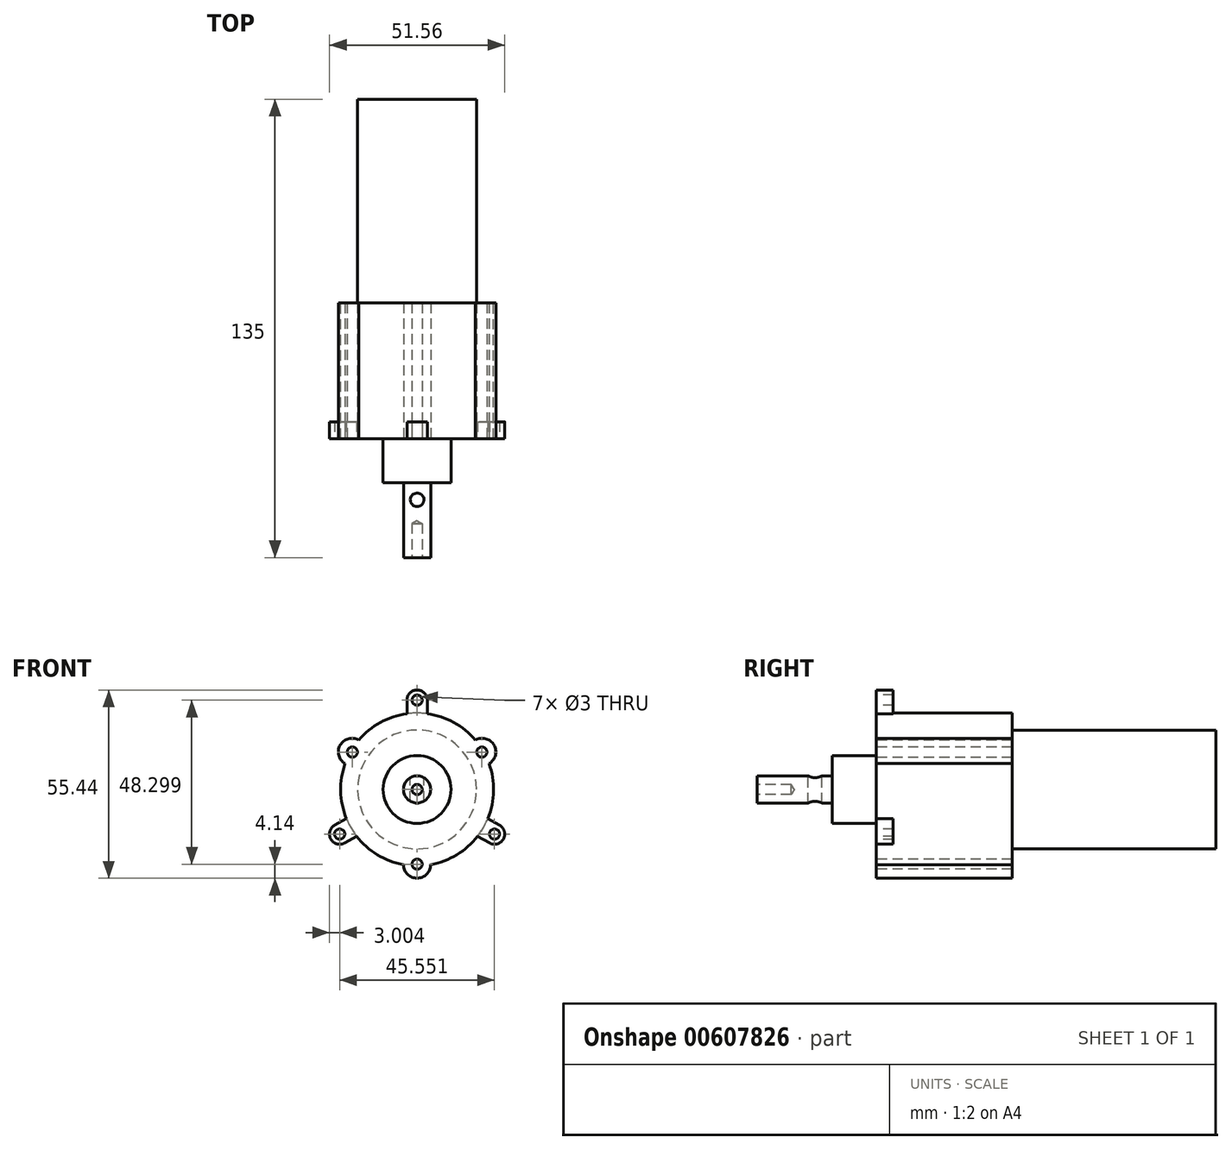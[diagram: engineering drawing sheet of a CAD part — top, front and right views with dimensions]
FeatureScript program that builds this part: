
annotation { "Feature Type Name" : "Feature", "Feature Type Description" : "" }
export const myFeature = defineFeature(function(context is Context, id is Id, definition is map)
    precondition{}
    {
        {
            var Q0;
            Q0=qCreatedBy(makeId("Front.planeOp"),FACE);
            var sketch = newSketch(context, id + "F0", { "sketchPlane" : qUnion([Q0])});
            skCircle(sketch, "E0", {"center": v(0, 0) * mm, "radius": 17.5 * mm});
            skSolve(sketch);
        }
        {
            var Q0;
            Q0 = qSketchRegion(id + "F0", true);
            extrude(context, id + "F1", {"entities" : qUnion([Q0]), "depth" : 60 * mm, "offsetDistance" : 25 * mm});
        }
        {
            var Q0;
            Q0=makeQuery(id+"F1.opExtrude","CAP_FACE",FACE,{"disambiguationData":[OSD([sQuery(id+"F0.wireOp",EDGE,"E0")])],"isStart":false});
            var sketch = newSketch(context, id + "F2", { "sketchPlane" : qUnion([Q0])});
            skCircle(sketch, "E1", {"center": v(0, 0) * mm, "radius": 22.5 * mm});
            skSolve(sketch);
        }
        {
            var Q0;
            Q0 = qSketchRegion(id + "F2", true);
            extrude(context, id + "F3", {"entities" : qUnion([Q0]), "operationType" : NewBodyOperationType.ADD, "depth" : 40 * mm, "offsetDistance" : 25 * mm});
        }
        {
            var Q0;
            Q0=makeQuery(id+"F3.opExtrude","CAP_FACE",FACE,{"disambiguationData":[OSD([sQuery(id+"F2.wireOp",EDGE,"E1")])],"isStart":false});
            var sketch = newSketch(context, id + "F4", { "sketchPlane" : qUnion([Q0])});
            skLineSegment(sketch, "E2", {"start": v(0, 0) * mm, "end": v(0, -22.5) * mm, "construction": true});
            skLineSegment(sketch, "E3", {"start": v(-4, -22.14) * mm, "end": v(4, -22.14) * mm});
            skArc(sketch, "E4", {"start": v(-4, -22.14) * mm, "mid": v(0, -26.14) * mm, "end": v(4, -22.14) * mm});
            skArc(sketch, "E5.1.0", {"start": v(21.18, 7.6) * mm, "mid": v(22.64, 13.07) * mm, "end": v(17.18, 14.53) * mm});
            skLineSegment(sketch, "E5.1.1", {"start": v(21.18, 7.6) * mm, "end": v(17.18, 14.53) * mm});
            skArc(sketch, "E5.2.0", {"start": v(-17.18, 14.53) * mm, "mid": v(-22.64, 13.07) * mm, "end": v(-21.18, 7.6) * mm});
            skLineSegment(sketch, "E5.2.1", {"start": v(-17.18, 14.53) * mm, "end": v(-21.18, 7.6) * mm});
            skPoint(sketch, "E5.center", {"position": v(0, 0) * mm});
            skSolve(sketch);
        }
        {
            var Q0;
            Q0 = qSketchRegion(id + "F4", true);
            extrude(context, id + "F5", {"entities" : qUnion([Q0]), "operationType" : NewBodyOperationType.ADD, "oppositeDirection" : true, "depth" : 40 * mm, "offsetDistance" : 25 * mm});
        }
        {
            var Q0;
            Q0=makeQuery(id+"F5.boolean.opBoolean","MERGE",FACE,{"derivedFrom":[makeQuery(id+"F3.opExtrude","CAP_FACE",FACE,{"disambiguationData":[OSD([sQuery(id+"F2.wireOp",EDGE,"E1")])],"isStart":false}),makeQuery(id+"F5.opExtrude","CAP_FACE",FACE,{"disambiguationData":[OSD([sQuery(id+"F4.wireOp",EDGE,"E3"),sQuery(id+"F4.wireOp",EDGE,"E4")])],"isStart":true})]});
            var sketch = newSketch(context, id + "F6", { "sketchPlane" : qUnion([Q0])});
            skPoint(sketch, "E6", {"position": v(0, -22) * mm});
            skPoint(sketch, "E7.1.0", {"position": v(19.05, 11) * mm});
            skPoint(sketch, "E7.2.0", {"position": v(-19.05, 11) * mm});
            skPoint(sketch, "E7.center", {"position": v(0, 0) * mm});
            skSolve(sketch);
        }
        {
            var Q0;
            Q0=sQuery(id+"F6.wireOp",VERTEX,"E7.2.0");
            var Q1;
            Q1=sQuery(id+"F6.wireOp",VERTEX,"E6");
            var Q2;
            Q2=sQuery(id+"F6.wireOp",VERTEX,"E7.1.0");
            var Q3;
            Q3=makeQuery(id+"F1.opExtrude","SWEPT_BODY",BODY,{"disambiguationData":[OSD([sQuery(id+"F0.wireOp",EDGE,"E0")])]});
            hole(context, id + "F7", {"style" : HoleStyle.SIMPLE, "endStyle" : HoleEndStyle.THROUGH, "holeDiameter" : 3 * mm, "majorDiameter" : 5 * mm, "isTappedThrough" : true, "tappedDepth" : 12 * mm, "tapClearance" : 3, "locations" : qUnion([Q0, Q1, Q2]), "scope" : qUnion([Q3])});
        }
        {
            var Q0;
            Q0=makeQuery(id+"F3.opExtrude","CAP_FACE",FACE,{"disambiguationData":[OSD([sQuery(id+"F2.wireOp",EDGE,"E1")])],"isStart":false});
            var sketch = newSketch(context, id + "F8", { "sketchPlane" : qUnion([Q0])});
            skLineSegment(sketch, "E8", {"start": v(0, 22.5) * mm, "end": v(0, -22.5) * mm, "construction": true});
            skLineSegment(sketch, "E9", {"start": v(-22.5, 0) * mm, "end": v(22.5, 0) * mm, "construction": true});
            skLineSegment(sketch, "E10", {"start": v(-3, 22.3) * mm, "end": v(-3, 26.3) * mm});
            skLineSegment(sketch, "E11", {"start": v(3, 26.3) * mm, "end": v(3, 22.3) * mm});
            skArc(sketch, "E12", {"start": v(3, 26.3) * mm, "mid": v(0, 29.3) * mm, "end": v(-3, 26.3) * mm});
            skLineSegment(sketch, "E13", {"start": v(-3, 22.3) * mm, "end": v(3, 22.3) * mm});
            skCircle(sketch, "E14", {"center": v(0, 26.3) * mm, "radius": 1.5 * mm});
            skArc(sketch, "E15.1.0", {"start": v(-24.28, -10.55) * mm, "mid": v(-25.37, -14.65) * mm, "end": v(-21.28, -15.75) * mm});
            skCircle(sketch, "E15.1.1", {"center": v(-22.78, -13.15) * mm, "radius": 1.5 * mm});
            skLineSegment(sketch, "E15.1.2", {"start": v(-24.28, -10.55) * mm, "end": v(-20.81, -8.55) * mm});
            skLineSegment(sketch, "E15.1.3", {"start": v(-17.81, -13.75) * mm, "end": v(-21.28, -15.75) * mm});
            skLineSegment(sketch, "E15.1.4", {"start": v(-17.81, -13.75) * mm, "end": v(-20.81, -8.55) * mm});
            skArc(sketch, "E15.2.0", {"start": v(21.28, -15.75) * mm, "mid": v(25.37, -14.65) * mm, "end": v(24.28, -10.55) * mm});
            skCircle(sketch, "E15.2.1", {"center": v(22.78, -13.15) * mm, "radius": 1.5 * mm});
            skLineSegment(sketch, "E15.2.2", {"start": v(21.28, -15.75) * mm, "end": v(17.81, -13.75) * mm});
            skLineSegment(sketch, "E15.2.3", {"start": v(20.81, -8.55) * mm, "end": v(24.28, -10.55) * mm});
            skLineSegment(sketch, "E15.2.4", {"start": v(20.81, -8.55) * mm, "end": v(17.81, -13.75) * mm});
            skPoint(sketch, "E15.center", {"position": v(0, 0) * mm});
            skSolve(sketch);
        }
        {
            var Q0;
            Q0 = qSketchRegion(id + "F8", true);
            extrude(context, id + "F9", {"entities" : qUnion([Q0]), "operationType" : NewBodyOperationType.ADD, "oppositeDirection" : true, "depth" : 5 * mm, "offsetDistance" : 25 * mm});
        }
        {
            var Q0;
            Q0=makeQuery(id+"F9.boolean.opBoolean","MERGE",FACE,{"derivedFrom":[makeQuery(id+"F5.boolean.opBoolean","MERGE",FACE,{"derivedFrom":[makeQuery(id+"F3.opExtrude","CAP_FACE",FACE,{"disambiguationData":[OSD([sQuery(id+"F2.wireOp",EDGE,"E1")])],"isStart":false}),makeQuery(id+"F5.opExtrude","CAP_FACE",FACE,{"disambiguationData":[OSD([sQuery(id+"F4.wireOp",EDGE,"E3"),sQuery(id+"F4.wireOp",EDGE,"E4")])],"isStart":true}),makeQuery(id+"F5.opExtrude","CAP_FACE",FACE,{"disambiguationData":[OSD([sQuery(id+"F4.wireOp",EDGE,"E5.1.0"),sQuery(id+"F4.wireOp",EDGE,"E5.1.1")])],"isStart":true}),makeQuery(id+"F5.opExtrude","CAP_FACE",FACE,{"disambiguationData":[OSD([sQuery(id+"F4.wireOp",EDGE,"E5.2.0"),sQuery(id+"F4.wireOp",EDGE,"E5.2.1")])],"isStart":true})]}),makeQuery(id+"F9.opExtrude","CAP_FACE",FACE,{"disambiguationData":[OSD([sQuery(id+"F8.wireOp",EDGE,"E10"),sQuery(id+"F8.wireOp",EDGE,"E11"),sQuery(id+"F8.wireOp",EDGE,"E12"),sQuery(id+"F8.wireOp",EDGE,"E13"),sQuery(id+"F8.wireOp",EDGE,"E14")])],"isStart":true}),makeQuery(id+"F9.opExtrude","CAP_FACE",FACE,{"disambiguationData":[OSD([sQuery(id+"F8.wireOp",EDGE,"E15.1.0"),sQuery(id+"F8.wireOp",EDGE,"E15.1.1"),sQuery(id+"F8.wireOp",EDGE,"E15.1.2"),sQuery(id+"F8.wireOp",EDGE,"E15.1.3"),sQuery(id+"F8.wireOp",EDGE,"E15.1.4")])],"isStart":true}),makeQuery(id+"F9.opExtrude","CAP_FACE",FACE,{"disambiguationData":[OSD([sQuery(id+"F8.wireOp",EDGE,"E15.2.0"),sQuery(id+"F8.wireOp",EDGE,"E15.2.1"),sQuery(id+"F8.wireOp",EDGE,"E15.2.2"),sQuery(id+"F8.wireOp",EDGE,"E15.2.3"),sQuery(id+"F8.wireOp",EDGE,"E15.2.4")])],"isStart":true})]});
            var sketch = newSketch(context, id + "F10", { "sketchPlane" : qUnion([Q0])});
            skCircle(sketch, "E16", {"center": v(0, 0) * mm, "radius": 10 * mm});
            skSolve(sketch);
        }
        {
            var Q0;
            Q0=makeQuery(id+"F10.imprint","IMPRINT",FACE,{"disambiguationData":[TD([[makeQuery(id+"F10.imprint","IMPRINT",EDGE,{"derivedFrom":sQuery(id+"F10.wireOp",EDGE,"E16")}),1.0]])]});
            extrude(context, id + "F11", {"entities" : qUnion([Q0]), "operationType" : NewBodyOperationType.ADD, "depth" : 13 * mm, "offsetDistance" : 25 * mm});
        }
        {
            var Q0;
            Q0=makeQuery(id+"F11.opExtrude","CAP_FACE",FACE,{"disambiguationData":[OSD([sQuery(id+"F10.wireOp",EDGE,"E16")])],"isStart":false});
            var sketch = newSketch(context, id + "F12", { "sketchPlane" : qUnion([Q0])});
            skCircle(sketch, "E17", {"center": v(0, 0) * mm, "radius": 4 * mm});
            skSolve(sketch);
        }
        {
            var Q0;
            Q0=makeQuery(id+"F12.imprint","IMPRINT",FACE,{"disambiguationData":[TD([[makeQuery(id+"F12.imprint","IMPRINT",EDGE,{"derivedFrom":sQuery(id+"F12.wireOp",EDGE,"E17")}),1.0]])]});
            var Q1;
            Q1=sQuery(id+"F12.wireOp",EDGE,"E17");
            extrude(context, id + "F13", {"entities" : qUnion([Q0]), "operationType" : NewBodyOperationType.ADD, "surfaceEntities" : qUnion([Q1]), "depth" : 22 * mm, "offsetDistance" : 25 * mm});
        }
        {
            var Q0;
            Q0=makeQuery(id+"F13.opExtrude","CAP_FACE",FACE,{"disambiguationData":[OSD([sQuery(id+"F12.wireOp",EDGE,"E17")])],"isStart":false});
            var sketch = newSketch(context, id + "F14", { "sketchPlane" : qUnion([Q0])});
            skPoint(sketch, "E18", {"position": v(0, 0) * mm});
            skSolve(sketch);
        }
        {
            var Q0;
            Q0=sQuery(id+"F14.wireOp",VERTEX,"E18");
            var Q1;
            Q1=makeQuery(id+"F1.opExtrude","SWEPT_BODY",BODY,{"disambiguationData":[OSD([sQuery(id+"F0.wireOp",EDGE,"E0")])]});
            hole(context, id + "F15", {"style" : HoleStyle.SIMPLE, "endStyle" : HoleEndStyle.BLIND, "holeDiameter" : 3 * mm, "majorDiameter" : 5 * mm, "holeDepth" : 10 * mm, "isTappedThrough" : true, "tappedDepth" : 12 * mm, "tapClearance" : 3, "locations" : qUnion([Q0]), "scope" : qUnion([Q1])});
        }
        {
            var Q0;
            Q0=qCreatedBy(makeId("Top.planeOp"),FACE);
            var sketch = newSketch(context, id + "F16", { "sketchPlane" : qUnion([Q0])});
            skPoint(sketch, "E19", {"position": v(0, -118) * mm});
            skCircle(sketch, "E20", {"center": v(0, -118) * mm, "radius": 2 * mm});
            skSolve(sketch);
        }
        {
            var Q0;
            Q0 = qSketchRegion(id + "F16", true);
            var Q1;
            Q1=sQuery(id+"F16.wireOp",EDGE,"E20");
            extrude(context, id + "F17", {"entities" : qUnion([Q0]), "operationType" : NewBodyOperationType.REMOVE, "surfaceEntities" : qUnion([Q1]), "endBound" : BoundingType.SYMMETRIC, "oppositeDirection" : true, "depth" : 25 * mm, "offsetDistance" : 25 * mm});
        }
    });
